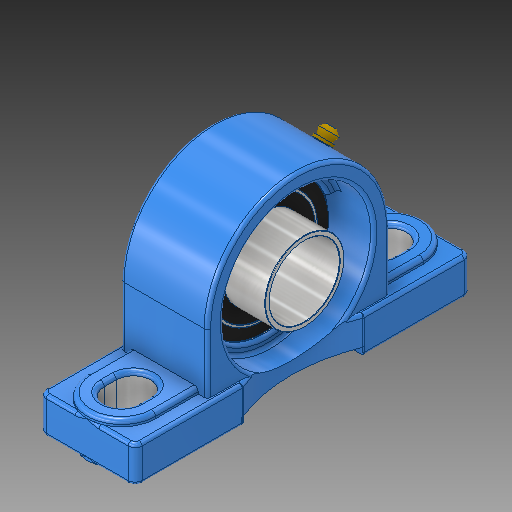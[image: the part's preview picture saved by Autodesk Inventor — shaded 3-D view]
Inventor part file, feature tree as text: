
AUTODESK INVENTOR PART (.ipt)
format: ipt  version: 2019 (Build 230136000, 136)  size: 680,448 bytes
history: native  units: in
note: dims shown in document units (in); Inventor stores cm internally (conversion verified against a paired STEP export)
features: sketch x28, plane x7, other x3
ambient origin geometry x8: Origin, YZ Plane, XZ Plane, XY Plane, X Axis, Y Axis, Z Axis, Center Point
bodies: Solid1 (feature_tree)
feature tree (38):
  other  "Pillow Bearing inventor_MIR.ipt"
  other  "Solid1::Pillow Bearing inventor_MIR.ipt"
  other  "TaggingFeature1"
  sketch  "Sketch1"  dims[d0=0.3937in]
  sketch  "Sketch2"
  sketch  "Sketch3"
  sketch  "Sketch4"
  sketch  "Sketch5"
  sketch  "Sketch6"
  sketch  "Sketch7"
  sketch  "Sketch8"
  sketch  "Sketch9"
  sketch  "Sketch10"
  sketch  "Sketch11"
  sketch  "Sketch13"
  sketch  "Sketch14"
  sketch  "Sketch15"
  sketch  "Sketch17"
  sketch  "Sketch18"
  sketch  "Sketch19"
  sketch  "Sketch20"
  sketch  "Sketch21"
  sketch  "Sketch22"
  sketch  "Sketch23"
  sketch  "Sketch24"
  sketch  "Sketch25"
  sketch  "Sketch26"
  sketch  "Sketch27"
  sketch  "Sketch28"
  sketch  "Sketch29"
  sketch  "Sketch30"
  plane  "Work Plane1"
  plane  "Work Plane2"
  plane  "Work Plane5"
  plane  "Work Plane6"
  plane  "Work Plane7"
  plane  "Work Plane8"
  plane  "Work Plane9"
